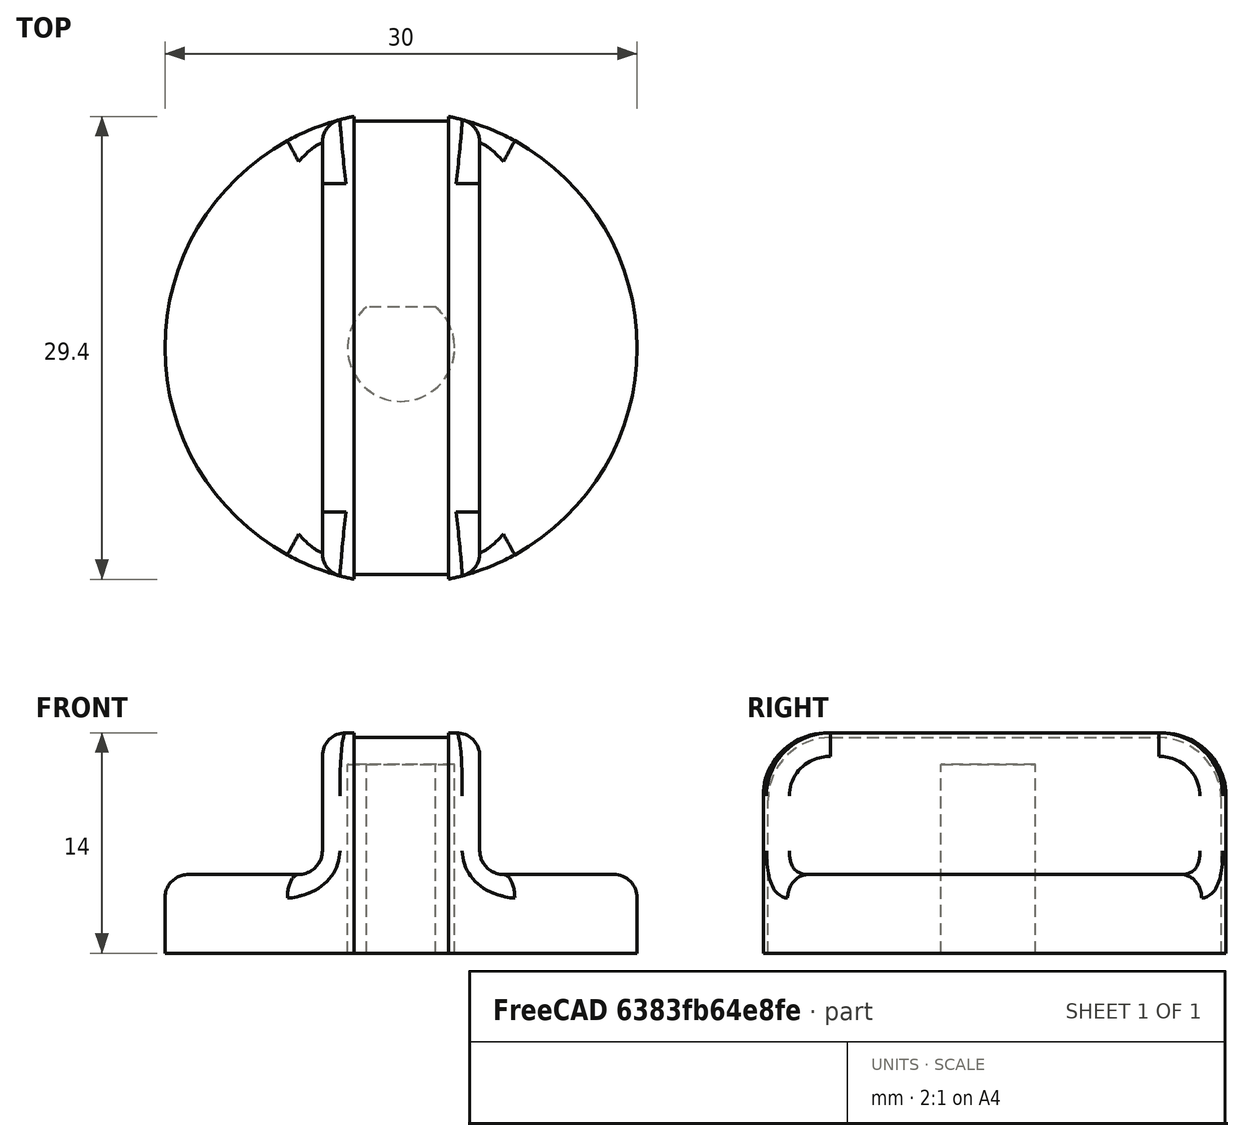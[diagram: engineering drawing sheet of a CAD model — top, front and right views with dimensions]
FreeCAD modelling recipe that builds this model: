
FCSTD DOCUMENT  (FreeCAD 0.17R13541 (Git))
Label: fuel knob
License: All rights reserved
LicenseURL: http://en.wikipedia.org/wiki/All_rights_reserved
objects: Part::Cut×9, Part::Box×8, Part::Cylinder×3, Part::Fillet×3, Part::Fuse×1
note: 24 computed .brp shape members not serialized (recipe doc carries the construction recipe); baked Part::Feature solids carry a one-line shape summary decoded from their .brp

FEATURE [Part::Cylinder] Cylinder  label="Cilindro"
  Angle = 360
  AttacherType = Attacher::AttachEngine3D
  Height = 12
  Radius = 15
FEATURE [Part::Box] Box  label="Recorte 1"
  AttacherType = Attacher::AttachEngine3D
  Height = 10
  Length = 15
  Placement = pos=(5,-15,3) rot=(0,0,1;0rad)
  Width = 35
FEATURE [Part::Box] Box001  label="Recorte 2"
  AttacherType = Attacher::AttachEngine3D
  Height = 10
  Length = 15
  Placement = pos=(-20,-15,3) rot=(0,0,1;0rad)
  Width = 35
FEATURE [Part::Cut] Cut
  Base = -> Cylinder
  Refine = true
  Tool = -> Box
FEATURE [Part::Cut] Cut001  label="Pieza cruda"
  Base = -> Cut
  Refine = true
  Tool = -> Box001
FEATURE [Part::Box] Box002  label="Cubo"
  AttacherType = Attacher::AttachEngine3D
  Height = 10
  Length = 6
  Placement = pos=(-3,-17,11.7) rot=(0,0,1;0rad)
  Width = 35
FEATURE [Part::Cut] Cut002
  Base = -> Cut001
  Refine = true
  Tool = -> Box002
FEATURE [Part::Box] Box003  label="Cubo001"
  AttacherType = Attacher::AttachEngine3D
  Height = 15
  Length = 6
  Placement = pos=(-3,14.4,-2) rot=(0,0,1;0rad)
  Width = 10
FEATURE [Part::Box] Box004  label="Cubo002"
  AttacherType = Attacher::AttachEngine3D
  Height = 15
  Length = 6
  Placement = pos=(-3,-24.4,-2) rot=(0,0,1;0rad)
  Width = 10
FEATURE [Part::Cut] Cut003
  Base = -> Cut002
  Refine = true
  Tool = -> Box003
FEATURE [Part::Cut] Cut004  label="Pieza con biel"
  Base = -> Cut003
  Refine = true
  Tool = -> Box004
FEATURE [Part::Cylinder] Cylinder001  label="Cilindro001"
  Angle = 360
  AttacherType = Attacher::AttachEngine3D
  Height = 2.5
  Placement = pos=(0,0,-2) rot=(0,0,1;0rad)
  Radius = 15
FEATURE [Part::Fuse] Fusion
  Base = -> Cut004
  Refine = true
  Tool = -> Cylinder001
FEATURE [Part::Box] Box005  label="Cubo003"
  AttacherType = Attacher::AttachEngine3D
  Height = 15
  Length = 6
  Placement = pos=(-3,-24.4,-2) rot=(0,0,1;0rad)
  Width = 10
FEATURE [Part::Box] Box006  label="Cubo004"
  AttacherType = Attacher::AttachEngine3D
  Height = 15
  Length = 6
  Placement = pos=(-3,14.4,-2) rot=(0,0,1;0rad)
  Width = 10
FEATURE [Part::Cut] Cut005
  Base = -> Fusion
  Refine = true
  Tool = -> Box005
FEATURE [Part::Cut] Cut006  label="Pieza sin cantear"
  Base = -> Cut005
  Refine = true
  Tool = -> Box006
FEATURE [Part::Cylinder] Cylinder002  label="Taladro"
  Angle = 360
  AttacherType = Attacher::AttachEngine3D
  Height = 13
  Placement = pos=(0,0,-26) rot=(0,0,1;0rad)
  Radius = 3.4
FEATURE [Part::Fillet] Fillet
  Base = -> Cut006
  Edges = 6 edges r=4: [Edge2,Edge3,Edge9,Edge10,Edge29,Edge32]
FEATURE [Part::Fillet] Fillet001
  Base = -> Fillet
  Edges = 2 edges r=1.5: [Edge55,Edge56]
FEATURE [Part::Fillet] Fillet002  label="Pieza final sin taladro"
  Base = -> Fillet001
  Edges = 2 edges r=1.5: [Edge13,Edge60]
FEATURE [Part::Box] Box007  label="Cubo005"
  AttacherType = Attacher::AttachEngine3D
  Height = 17
  Length = 10
  Placement = pos=(-5,2.6,-28) rot=(0,0,1;0rad)
  Width = 10
FEATURE [Part::Cut] Cut007
  Base = -> Cylinder002
  Placement = pos=(0,0,23) rot=(0,0,1;0rad)
  Refine = true
  Tool = -> Box007
FEATURE [Part::Cut] Cut008  label="Fuel knob"
  Base = -> Fillet002
  Refine = true
  Tool = -> Cut007
